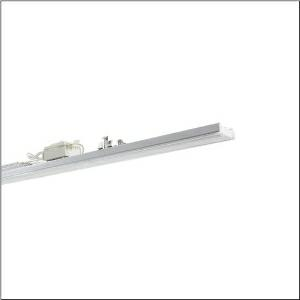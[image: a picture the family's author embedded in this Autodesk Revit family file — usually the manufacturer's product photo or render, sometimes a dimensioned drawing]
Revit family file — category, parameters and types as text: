
# Revit family: licross_r__21_recessed_mo_52tl18dn495g_5e12
name_source: partatom
category: Lighting Fixtures
units: mm (PartAtom-declared; Revit-internal decimal feet)

## family parameters
Cut with Voids When Loaded = No
Host = Face
Light Source = No
Part Type = Normal
Room Calculation Point = No
Round Connector Dimension = Use Diameter
Shared = No

## types (1)
- --- (1 x LED, 9990 lm, 58 W, 4000K)
    Apparent Load = 58 VA
    CIE Flux Codes = 79 95 99 100 100
    Color Rendering = 80
    Color Temperature = 4000K
    Default Elevation = 1800 mm
    Description = Licross® 21 Recessed MO, luminaire insert, of sheet steel, galvanised, coil coated, white, length: 1.500mm, width: 66mm, height: 67mm, LED rated luminous flux: 9.990lm, light colour: 840, control gear: DALI 2, with plug, 5-pole, with phase selection, mains connection: 220..240V, AC, 50/60Hz, rated input power: 58W, halogen-free wiring, primary light control with lens, of plastic, primary optical cover: cover, of PMMA, light emission: direct distribution, primary light characteristic: symmetric, protection rating (complete): IP40, insulation class (complete): insulation class I (protective earthing), certification: CE, ENEC, VDE, UKCA, protection symbol: D if used in an environment without relevant dust loads with corresponding accessories, impact resistance: IK06, permissible ambient temperature for indoor applications: -25..+35°C, corresponds to IFS (International Featured Standards) requirements for safety and quality in the food industry, reducing of maximum allowable ambient temperature of 5°C with ceiling mounting, LABS conformity tested according to VDMA 24364:2018-05, packaging unit: 1 piece
    Height = 58 mm
    Lamp = 1 x LED
    Lamp Light Flux = 9990 lm
    Lamp Power = 58 W
    Lamp count = 1
    Length = 1500 mm
    Luminous efficacy = 172 lm/W
    Manufacturer = Siteco
    ModVariant = No
    Model = 52TL18DN495G
    Mounting Place = Ceiling
    Mounting Type = Pendant
    Number of Poles = 1
    OnlyDefault = Yes
    Power Factor = 1
    Product Name = Licross® 21 Recessed MO
    Product group = luminaire insert
    ProductGroupID = 902
    Protection Class = Protection class I
    Protection Degree = IP 40
    RLX_Detail_Level = 1
    RLX_Emergency_Light_Flux = 0 lm
    RLX_Emergency_Type = 0
    RLX_Emergency_Type_DB = No
    RlxData = <blob elided: 24573 chars, md5=f02ec218>
    Socket = socket
    Standby Power = 0 W
    System Light Flux = 9990 lm
    System Power = 58 W
    Type Comments = factory setting: luminous flux: 100 % | dim-lin: 254 | 390 mA
    Type Image = l_1296930.jpg
    URL = http://relux.com
    VarID = @adj_125966
    Voltage = 0 V
    Weight = 0.00 kg
    Width = 66 mm

## geometry (parser evidence)
native form markers: Blend x4, Sweep x10
no freeform markers — native parametric forms only
